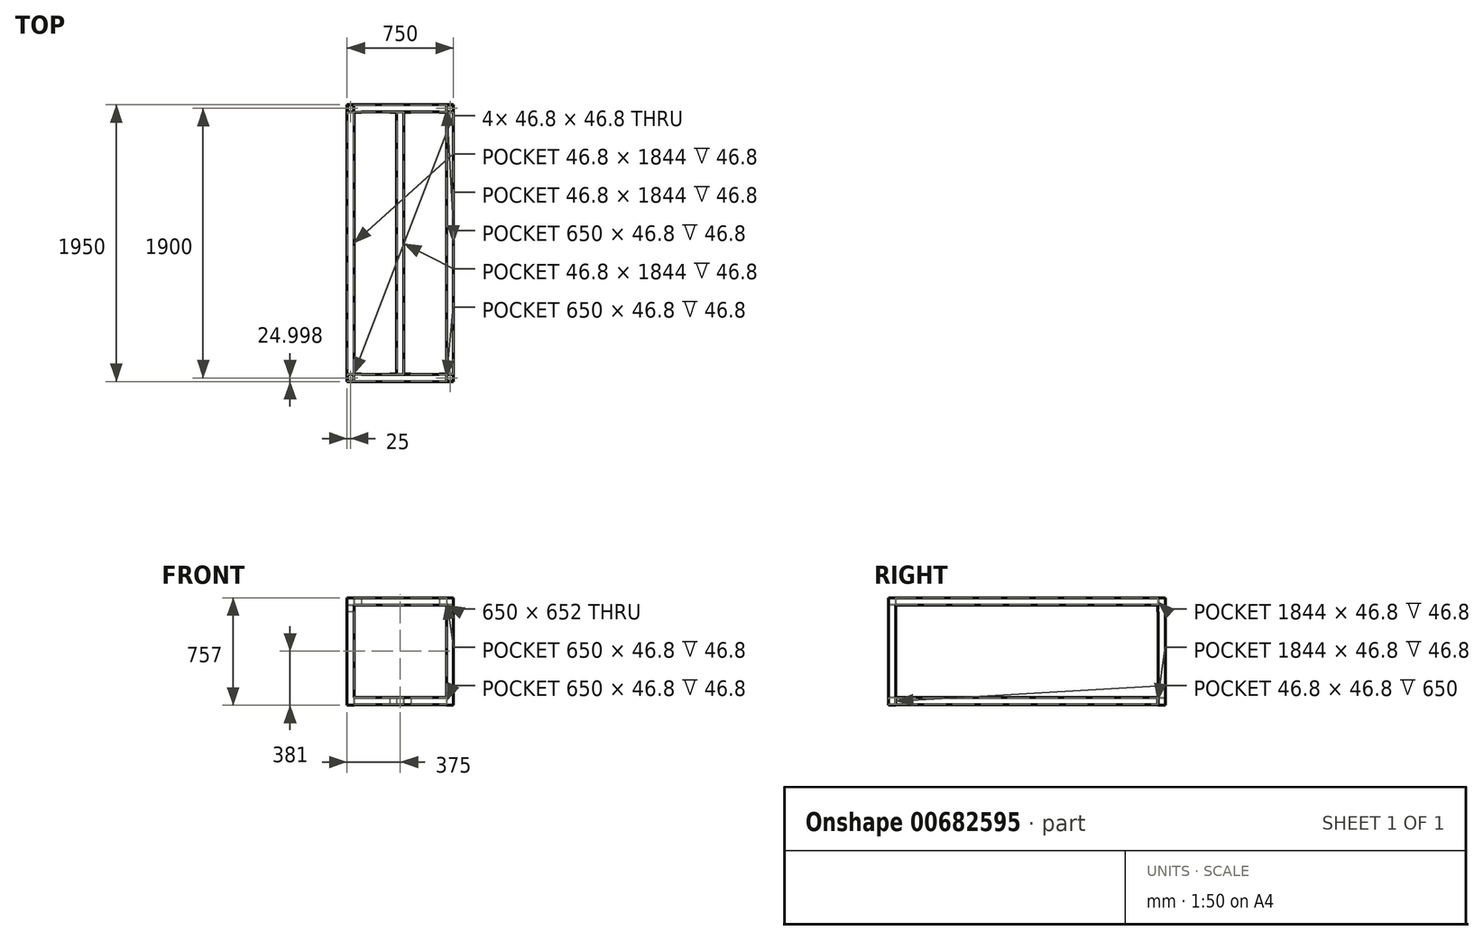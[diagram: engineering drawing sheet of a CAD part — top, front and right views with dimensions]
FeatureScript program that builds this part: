
annotation { "Feature Type Name" : "Feature", "Feature Type Description" : "" }
export const myFeature = defineFeature(function(context is Context, id is Id, definition is map)
    precondition{}
    {
        {
            var Q0;
            Q0=qCreatedBy(makeId("Top.planeOp"),FACE);
            var sketch = newSketch(context, id + "F0", { "sketchPlane" : qUnion([Q0])});
            skLineSegment(sketch, "E0.bottom", {"start": v(-50, 66.52) * mm, "end": v(0, 66.52) * mm});
            skLineSegment(sketch, "E0.top", {"start": v(-50, 16.52) * mm, "end": v(0, 16.52) * mm});
            skLineSegment(sketch, "E0.left", {"start": v(-50, 66.52) * mm, "end": v(-50, 16.52) * mm});
            skLineSegment(sketch, "E0.right", {"start": v(0, 66.52) * mm, "end": v(0, 16.52) * mm});
            skLineSegment(sketch, "E1.bottom", {"start": v(-48.4, 64.92) * mm, "end": v(-1.6, 64.92) * mm});
            skLineSegment(sketch, "E1.top", {"start": v(-48.4, 18.12) * mm, "end": v(-1.6, 18.12) * mm});
            skLineSegment(sketch, "E1.left", {"start": v(-48.4, 64.92) * mm, "end": v(-48.4, 18.12) * mm});
            skLineSegment(sketch, "E1.right", {"start": v(-1.6, 64.92) * mm, "end": v(-1.6, 18.12) * mm});
            skSolve(sketch);
        }
        {
            var Q0;
            Q0=qSketchRegion(id+"F0",true);
            extrude(context, id + "F1", {"entities" : qUnion([Q0]), "depth" : 757 * mm, "offsetDistance" : 25 * mm});
        }
        {
            var Q0;
            Q0=makeQuery(id+"F1.opExtrude","SWEPT_FACE",FACE,{"disambiguationData":[OSD([sQuery(id+"F0.wireOp",EDGE,"E0.right")])]});
            var sketch = newSketch(context, id + "F2", { "sketchPlane" : qUnion([Q0])});
            skLineSegment(sketch, "E2.bottom", {"start": v(16.52, 757) * mm, "end": v(66.52, 757) * mm});
            skLineSegment(sketch, "E2.top", {"start": v(16.52, 707) * mm, "end": v(66.52, 707) * mm});
            skLineSegment(sketch, "E2.left", {"start": v(16.52, 757) * mm, "end": v(16.52, 707) * mm});
            skLineSegment(sketch, "E2.right", {"start": v(66.52, 757) * mm, "end": v(66.52, 707) * mm});
            skLineSegment(sketch, "E3.bottom", {"start": v(18.12, 755.4) * mm, "end": v(64.92, 755.4) * mm});
            skLineSegment(sketch, "E3.top", {"start": v(18.12, 708.6) * mm, "end": v(64.92, 708.6) * mm});
            skLineSegment(sketch, "E3.left", {"start": v(18.12, 755.4) * mm, "end": v(18.12, 708.6) * mm});
            skLineSegment(sketch, "E3.right", {"start": v(64.92, 755.4) * mm, "end": v(64.92, 708.6) * mm});
            skLineSegment(sketch, "E4.bottom", {"start": v(16.52, 55) * mm, "end": v(66.52, 55) * mm});
            skLineSegment(sketch, "E4.top", {"start": v(16.52, 5) * mm, "end": v(66.52, 5) * mm});
            skLineSegment(sketch, "E4.left", {"start": v(16.52, 55) * mm, "end": v(16.52, 5) * mm});
            skLineSegment(sketch, "E4.right", {"start": v(66.52, 55) * mm, "end": v(66.52, 5) * mm});
            skLineSegment(sketch, "E5.bottom", {"start": v(18.12, 53.4) * mm, "end": v(64.92, 53.4) * mm});
            skLineSegment(sketch, "E5.top", {"start": v(18.12, 6.6) * mm, "end": v(64.92, 6.6) * mm});
            skLineSegment(sketch, "E5.left", {"start": v(18.12, 53.4) * mm, "end": v(18.12, 6.6) * mm});
            skLineSegment(sketch, "E5.right", {"start": v(64.92, 53.4) * mm, "end": v(64.92, 6.6) * mm});
            skSolve(sketch);
        }
        {
            var Q0;
            Q0=qSketchRegion(id+"F2",true);
            extrude(context, id + "F3", {"entities" : qUnion([Q0]), "operationType" : NewBodyOperationType.ADD, "depth" : 325 * mm, "offsetDistance" : 25 * mm});
        }
        {
            var Q0;
            Q0=makeQuery(id+"F3.boolean.opBoolean","MERGE",FACE,{"derivedFrom":[makeQuery(id+"F1.opExtrude","SWEPT_FACE",FACE,{"disambiguationData":[OSD([sQuery(id+"F0.wireOp",EDGE,"E0.top")])]}),makeQuery(id+"F3.opExtrude","SWEPT_FACE",FACE,{"disambiguationData":[OSD([sQuery(id+"F2.wireOp",EDGE,"E2.left")])]}),makeQuery(id+"F3.opExtrude","SWEPT_FACE",FACE,{"disambiguationData":[OSD([sQuery(id+"F2.wireOp",EDGE,"E4.left")])]})]});
            var sketch = newSketch(context, id + "F4", { "sketchPlane" : qUnion([Q0])});
            skLineSegment(sketch, "E6", {"start": v(-50, 757) * mm, "end": v(50, 757) * mm});
            skLineSegment(sketch, "E7", {"start": v(50, 757) * mm, "end": v(50, 707) * mm});
            skLineSegment(sketch, "E8", {"start": v(50, 707) * mm, "end": v(0, 707) * mm});
            skLineSegment(sketch, "E9", {"start": v(0, 707) * mm, "end": v(0, 657) * mm});
            skLineSegment(sketch, "E10", {"start": v(0, 657) * mm, "end": v(-50, 657) * mm});
            skLineSegment(sketch, "E11", {"start": v(-50, 657) * mm, "end": v(-50, 757) * mm});
            skLineSegment(sketch, "E12.bottom", {"start": v(325, 55) * mm, "end": v(250, 55) * mm});
            skLineSegment(sketch, "E12.top", {"start": v(325, 5) * mm, "end": v(250, 5) * mm});
            skLineSegment(sketch, "E12.left", {"start": v(325, 55) * mm, "end": v(325, 5) * mm});
            skLineSegment(sketch, "E12.right", {"start": v(250, 55) * mm, "end": v(250, 5) * mm});
            skSolve(sketch);
        }
        {
            var Q0;
            Q0=qSketchRegion(id+"F4",true);
            extrude(context, id + "F5", {"entities" : qUnion([Q0]), "operationType" : NewBodyOperationType.ADD, "depth" : 3 * mm, "offsetDistance" : 25 * mm});
        }
        {
            var Q0;
            Q0=makeQuery(id+"F5.opExtrude","CAP_FACE",FACE,{"disambiguationData":[OSD([sQuery(id+"F4.wireOp",EDGE,"E6"),sQuery(id+"F4.wireOp",EDGE,"E7"),sQuery(id+"F4.wireOp",EDGE,"E8"),sQuery(id+"F4.wireOp",EDGE,"E9"),sQuery(id+"F4.wireOp",EDGE,"E10"),sQuery(id+"F4.wireOp",EDGE,"E11")])],"isStart":false});
            var sketch = newSketch(context, id + "F6", { "sketchPlane" : qUnion([Q0])});
            skLineSegment(sketch, "E13.bottom", {"start": v(-50, 757) * mm, "end": v(0, 757) * mm});
            skLineSegment(sketch, "E13.top", {"start": v(-50, 707) * mm, "end": v(0, 707) * mm});
            skLineSegment(sketch, "E13.left", {"start": v(-50, 757) * mm, "end": v(-50, 707) * mm});
            skLineSegment(sketch, "E13.right", {"start": v(0, 757) * mm, "end": v(0, 707) * mm});
            skLineSegment(sketch, "E14.bottom", {"start": v(-48.4, 755.4) * mm, "end": v(-1.6, 755.4) * mm});
            skLineSegment(sketch, "E14.top", {"start": v(-48.4, 708.6) * mm, "end": v(-1.6, 708.6) * mm});
            skLineSegment(sketch, "E14.left", {"start": v(-48.4, 755.4) * mm, "end": v(-48.4, 708.6) * mm});
            skLineSegment(sketch, "E14.right", {"start": v(-1.6, 755.4) * mm, "end": v(-1.6, 708.6) * mm});
            skSolve(sketch);
        }
        {
            var Q0;
            Q0=qSketchRegion(id+"F6",true);
            extrude(context, id + "F7", {"entities" : qUnion([Q0]), "operationType" : NewBodyOperationType.ADD, "depth" : 922 * mm, "offsetDistance" : 25 * mm});
        }
        {
            var Q0;
            Q0=makeQuery(id+"F5.opExtrude","CAP_FACE",FACE,{"disambiguationData":[OSD([sQuery(id+"F4.wireOp",EDGE,"E12.bottom"),sQuery(id+"F4.wireOp",EDGE,"E12.top"),sQuery(id+"F4.wireOp",EDGE,"E12.left"),sQuery(id+"F4.wireOp",EDGE,"E12.right")])],"isStart":false});
            var sketch = newSketch(context, id + "F8", { "sketchPlane" : qUnion([Q0])});
            skLineSegment(sketch, "E15", {"start": v(325, 55) * mm, "end": v(300, 55) * mm});
            skLineSegment(sketch, "E16", {"start": v(300, 55) * mm, "end": v(300, 5) * mm});
            skLineSegment(sketch, "E17", {"start": v(300, 5) * mm, "end": v(325, 5) * mm});
            skLineSegment(sketch, "E18", {"start": v(325, 5) * mm, "end": v(325, 6.6) * mm});
            skLineSegment(sketch, "E19", {"start": v(325, 6.6) * mm, "end": v(301.6, 6.6) * mm});
            skLineSegment(sketch, "E20", {"start": v(301.6, 6.6) * mm, "end": v(301.6, 53.4) * mm});
            skLineSegment(sketch, "E21", {"start": v(301.6, 53.4) * mm, "end": v(325, 53.4) * mm});
            skLineSegment(sketch, "E22", {"start": v(325, 53.4) * mm, "end": v(325, 55) * mm});
            skSolve(sketch);
        }
        {
            var Q0;
            Q0=qSketchRegion(id+"F8",true);
            extrude(context, id + "F9", {"entities" : qUnion([Q0]), "operationType" : NewBodyOperationType.ADD, "flatOperationType" : FlatOperationType.REMOVE, "depth" : 922 * mm, "offsetDistance" : 25 * mm, "domain" : OperationDomain.MODEL});
        }
        {
            var Q0;
            Q0=makeQuery(id+"F1.opExtrude","SWEPT_BODY",BODY,{"disambiguationData":[OSD([sQuery(id+"F0.wireOp",EDGE,"E0.bottom"),sQuery(id+"F0.wireOp",EDGE,"E0.top"),sQuery(id+"F0.wireOp",EDGE,"E0.left"),sQuery(id+"F0.wireOp",EDGE,"E0.right"),sQuery(id+"F0.wireOp",EDGE,"E1.bottom"),sQuery(id+"F0.wireOp",EDGE,"E1.top"),sQuery(id+"F0.wireOp",EDGE,"E1.left"),sQuery(id+"F0.wireOp",EDGE,"E1.right")])]});
            var Q1;
            Q1=makeQuery(id+"F9.boolean.opBoolean","MERGE",FACE,{"derivedFrom":[makeQuery(id+"F5.boolean.opBoolean","MERGE",FACE,{"derivedFrom":[makeQuery(id+"F3.opExtrude","CAP_FACE",FACE,{"disambiguationData":[OSD([sQuery(id+"F2.wireOp",EDGE,"E4.bottom"),sQuery(id+"F2.wireOp",EDGE,"E4.top"),sQuery(id+"F2.wireOp",EDGE,"E4.left"),sQuery(id+"F2.wireOp",EDGE,"E4.right"),sQuery(id+"F2.wireOp",EDGE,"E5.bottom"),sQuery(id+"F2.wireOp",EDGE,"E5.top"),sQuery(id+"F2.wireOp",EDGE,"E5.left"),sQuery(id+"F2.wireOp",EDGE,"E5.right")])],"isStart":false}),makeQuery(id+"F5.opExtrude","SWEPT_FACE",FACE,{"disambiguationData":[OSD([sQuery(id+"F4.wireOp",EDGE,"E12.left")])]})]}),makeQuery(id+"F9.opExtrude","SWEPT_FACE",FACE,{"disambiguationData":[OSD([sQuery(id+"F8.wireOp",EDGE,"E18")])]}),makeQuery(id+"F9.opExtrude","SWEPT_FACE",FACE,{"disambiguationData":[OSD([sQuery(id+"F8.wireOp",EDGE,"E22")])]})]});
            mirror(context, id + "F10", {"operationType" : NewBodyOperationType.ADD, "entities" : qUnion([Q0]), "mirrorPlane" : qUnion([Q1])});
        }
        {
            var Q0;
            Q0=makeQuery(id+"F1.opExtrude","SWEPT_BODY",BODY,{"disambiguationData":[OSD([sQuery(id+"F0.wireOp",EDGE,"E0.bottom"),sQuery(id+"F0.wireOp",EDGE,"E0.top"),sQuery(id+"F0.wireOp",EDGE,"E0.left"),sQuery(id+"F0.wireOp",EDGE,"E0.right"),sQuery(id+"F0.wireOp",EDGE,"E1.bottom"),sQuery(id+"F0.wireOp",EDGE,"E1.top"),sQuery(id+"F0.wireOp",EDGE,"E1.left"),sQuery(id+"F0.wireOp",EDGE,"E1.right")])]});
            var Q1;
            {var subQ0=makeQuery(id+"F9.opExtrude","CAP_FACE",FACE,{"disambiguationData":[OSD([sQuery(id+"F8.wireOp",EDGE,"E15"),sQuery(id+"F8.wireOp",EDGE,"E16"),sQuery(id+"F8.wireOp",EDGE,"E17"),sQuery(id+"F8.wireOp",EDGE,"E18"),sQuery(id+"F8.wireOp",EDGE,"E19"),sQuery(id+"F8.wireOp",EDGE,"E20"),sQuery(id+"F8.wireOp",EDGE,"E21"),sQuery(id+"F8.wireOp",EDGE,"E22")])],"isStart":false});Q1=makeQuery(id+"F10.boolean.opBoolean","MERGE",FACE,{"derivedFrom":[subQ0,makeQuery(id+"F10.opPattern","COPY",FACE,{"derivedFrom":subQ0,"instanceName":"1"})]});}
            mirror(context, id + "F11", {"operationType" : NewBodyOperationType.ADD, "entities" : qUnion([Q0]), "mirrorPlane" : qUnion([Q1])});
        }
    });
